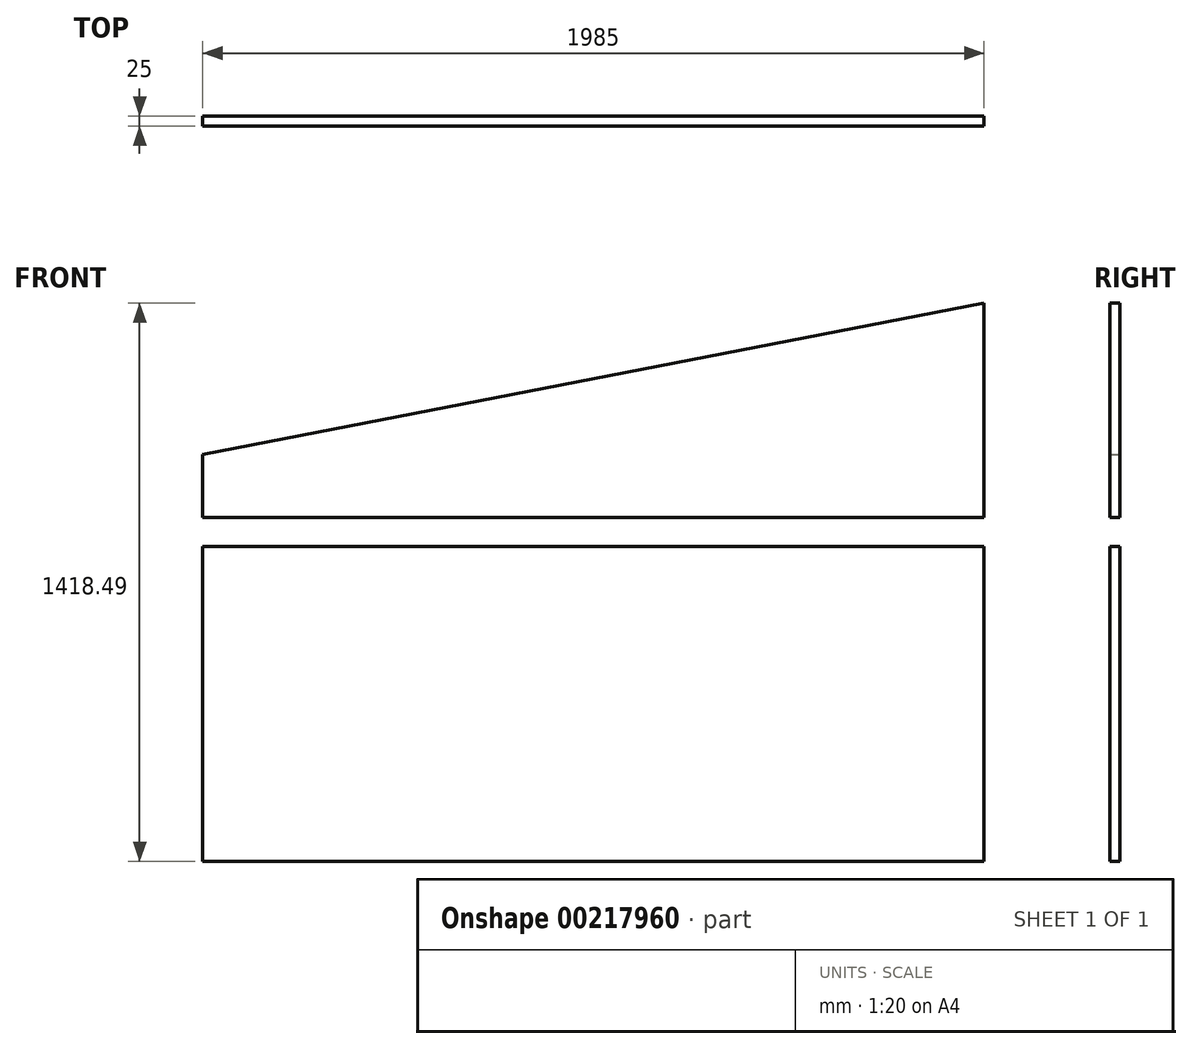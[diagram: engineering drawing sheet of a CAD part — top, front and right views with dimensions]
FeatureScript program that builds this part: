
annotation { "Feature Type Name" : "Feature", "Feature Type Description" : "" }
export const myFeature = defineFeature(function(context is Context, id is Id, definition is map)
    precondition{}
    {
        {
            var Q0;
            Q0=qCreatedBy(makeId("Front.planeOp"),FACE);
            var sketch = newSketch(context, id + "F0", { "sketchPlane" : qUnion([Q0])});
            skLineSegment(sketch, "E0", {"start": v(0, 0) * mm, "end": v(0, -160) * mm});
            skLineSegment(sketch, "E1", {"start": v(0, -160) * mm, "end": v(1985, -160) * mm});
            skLineSegment(sketch, "E2", {"start": v(1985, -160) * mm, "end": v(1985, 385) * mm});
            skLineSegment(sketch, "E3", {"start": v(1985, 385) * mm, "end": v(0, 0) * mm});
            skLineSegment(sketch, "E4.bottom", {"start": v(0, -233.49) * mm, "end": v(1985, -233.49) * mm});
            skLineSegment(sketch, "E4.top", {"start": v(0, -1033.49) * mm, "end": v(1985, -1033.49) * mm});
            skLineSegment(sketch, "E4.left", {"start": v(0, -233.49) * mm, "end": v(0, -1033.49) * mm});
            skLineSegment(sketch, "E4.right", {"start": v(1985, -233.49) * mm, "end": v(1985, -1033.49) * mm});
            skSolve(sketch);
        }
        {
            var Q0;
            Q0=makeQuery(id+"F0.imprint","IMPRINT",FACE,{"disambiguationData":[TD([[makeQuery(id+"F0.imprint","IMPRINT",EDGE,{"derivedFrom":sQuery(id+"F0.wireOp",EDGE,"E0")}),1.0]])]});
            var Q1;
            Q1=makeQuery(id+"F0.imprint","IMPRINT",FACE,{"disambiguationData":[TD([[makeQuery(id+"F0.imprint","IMPRINT",EDGE,{"derivedFrom":sQuery(id+"F0.wireOp",EDGE,"E4.bottom")}),-1.0]])]});
            extrude(context, id + "F1", {"entities" : qUnion([Q0, Q1]), "depth" : 25 * mm});
        }
    });
